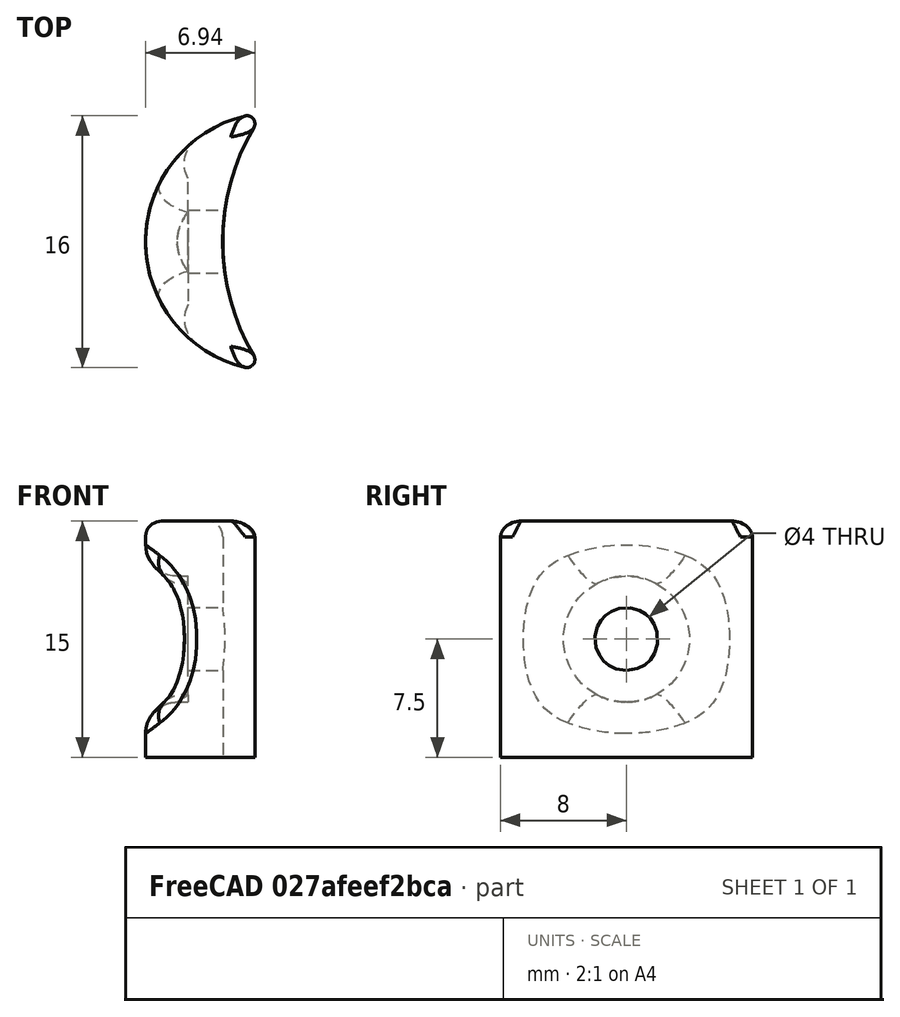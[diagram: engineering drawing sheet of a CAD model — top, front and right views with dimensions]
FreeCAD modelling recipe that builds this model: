
FCSTD DOCUMENT  (FreeCAD 0.16R)
Label: bouncySCrews
License: All rights reserved
LicenseURL: http://en.wikipedia.org/wiki/All_rights_reserved
objects: PartDesign::Fillet×3, Part::Cylinder×2, Part::Cut×2, Sketcher::SketchObject×1, PartDesign::Pad×1, Mesh::Feature×1
note: 10 computed .brp shape members not serialized (recipe doc carries the construction recipe); baked Part::Feature solids carry a one-line shape summary decoded from their .brp

FEATURE [Sketcher::SketchObject] Sketch
  sketch-geometry (2):
    g0: ArcOfCircle CenterX=0 CenterY=0 CenterZ=0 NormalX=0 NormalY=0 NormalZ=1 Radius=14.3 StartAngle=2.53358 EndAngle=3.7496
    g1: ArcOfCircle CenterX=-11 CenterY=0 CenterZ=0 NormalX=0 NormalY=0 NormalZ=1 Radius=8.20184 StartAngle=1.66081 EndAngle=4.62238
  constraints (6):
    c: Coincident(g0,g-1)
    c: PointOnObject(g1,g-1)
    c: Coincident(g1,g0)
    c: Coincident(g0,g1)
    c: Radius(g0) = 14.3
    c: DistanceX(g1) = -11
FEATURE [PartDesign::Pad] Pad
  Length = 15
  Length2 = 100
  Midplane = true
  Sketch = -> Sketch
  Type = 0
FEATURE [PartDesign::Fillet] Fillet
  Base = -> Pad [Edge1,Edge2]
  Radius = 0.5
FEATURE [Part::Cylinder] Cylinder
  Angle = 360
  Height = 10
  Placement = pos=(-23,0,0) rot=(0,1,0;1.5708rad)
  Radius = 2
FEATURE [Part::Cylinder] Cylinder001
  Angle = 360
  Height = 10
  Placement = pos=(-26.5,0,0) rot=(0,1,0;1.5708rad)
  Radius = 4
FEATURE [Part::Cut] Cut
  Base = -> Fillet
  Tool = -> Cylinder001
FEATURE [Part::Cut] Cut001
  Base = -> Cut
  Tool = -> Cylinder
FEATURE [PartDesign::Fillet] Fillet001
  Base = -> Cut001 [Edge16]
  Radius = 2
FEATURE [PartDesign::Fillet] Fillet002
  Base = -> Fillet001 [Edge9]
  Radius = 1
FEATURE [Mesh::Feature] Mesh  label="Fillet002 (Meshed)"
